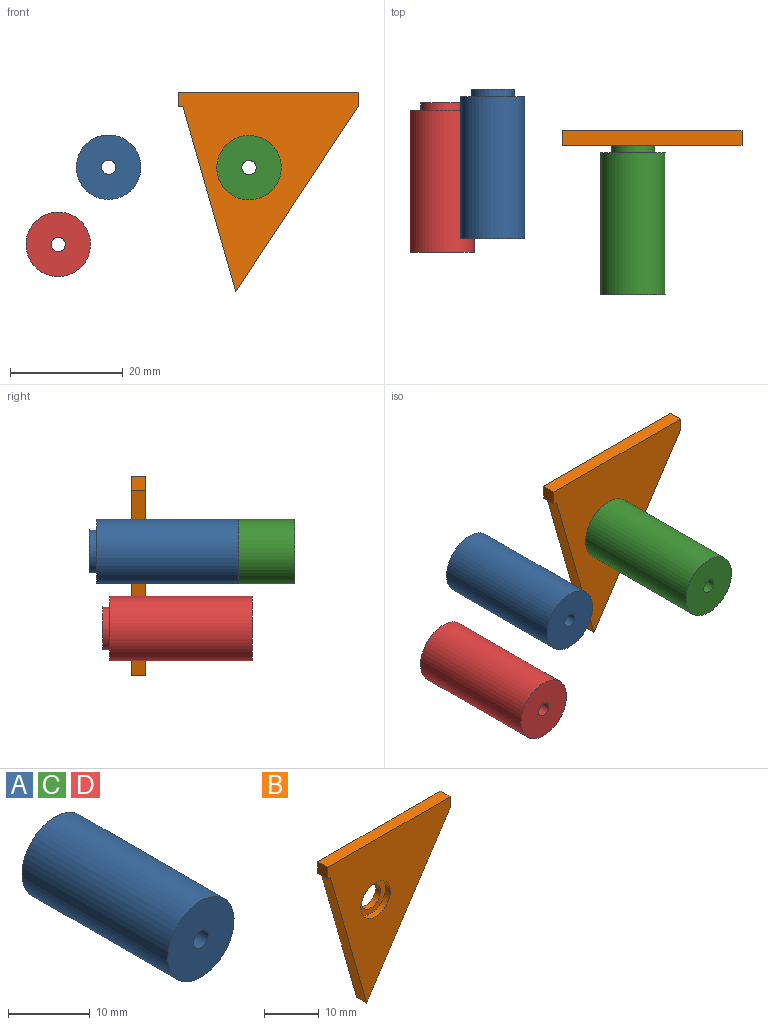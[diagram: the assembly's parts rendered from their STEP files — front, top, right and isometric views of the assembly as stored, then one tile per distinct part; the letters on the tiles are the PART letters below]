
ASSEMBLY  parts=4 mates=1
PART A: 6 faces, bbox 11.4x26.4x11.4 mm
  f0: plane 7.62x7.62mm, normal (0,1,0), area 40.5mm2, adj f2,f5
  f1: cylinder r=5.71mm len=25.17mm, axis (0,1,0), area 903.9mm2, adj f3,f4
  f2: cylinder r=1.27mm len=26.44mm, axis (0,1,0), area 211mm2, adj f0,f3
  f3: plane 11.43x11.43mm, normal (0,-1,0), area 97.5mm2, adj f1,f2
  f4: plane 11.43x11.43mm, normal (0,1,0), area 57mm2, adj f1,f5
  f5: cylinder r=3.81mm len=7.62mm, axis (0,-1,0), area 30.4mm2, adj f0,f4
PART B: 11 faces, bbox 31.8x2.5x35.4 mm
  f0: cylinder r=2.54mm len=5.08mm, axis (0,1,0), area 20.3mm2, adj f8,f10
  f1: plane 2.54x2.54mm, normal (-1,0,0), area 6.5mm2, adj f2,f6,f7,f8
  f2: plane 2.54x0.72mm, normal (0,0,-1), area 1.8mm2, adj f1,f3,f7,f8
  f3: plane 32.88x9.37mm, normal (-0.96,0,-0.27), area 86.8mm2, adj f2,f4,f7,f8
  f4: plane 32.88x21.66mm, normal (0.84,0,-0.55), area 100mm2, adj f3,f5,f7,f8
  f5: plane 2.54x2.54mm, normal (1,0,0), area 6.5mm2, adj f4,f6,f7,f8
  f6: plane 31.75x2.54mm, normal (0,0,1), area 80.6mm2, adj f1,f5,f7,f8
  f7: plane 35.42x31.75mm, normal (0,-1,0), area 545.1mm2, adj f1,f2,f3,f4,f5,f6,f9
  f8: plane 35.42x31.75mm, normal (0,1,0), area 570.4mm2, adj f0,f1,f2,f3,f4,f5,f6
  f9: cylinder r=3.81mm len=7.62mm, axis (0,-1,0), area 30.4mm2, adj f7,f10
  f10: plane 7.62x7.62mm, normal (0,-1,0), area 25.3mm2, adj f0,f9
PART C: same geometry as A
PART D: same geometry as A
PLACE A t=(73.87,17.71,27.61)mm
PLACE B t=(98.77,9.06,27.53)mm
PLACE C rot(axis=(0,1,0),90deg) t=(11.85,7.79,-35.16)mm
PLACE D t=(64.94,15.34,13.93)mm
MATE fastened C.f1 <-> B.f0  axis (0,1,0) through (23.96,6.52,39.64)mm
